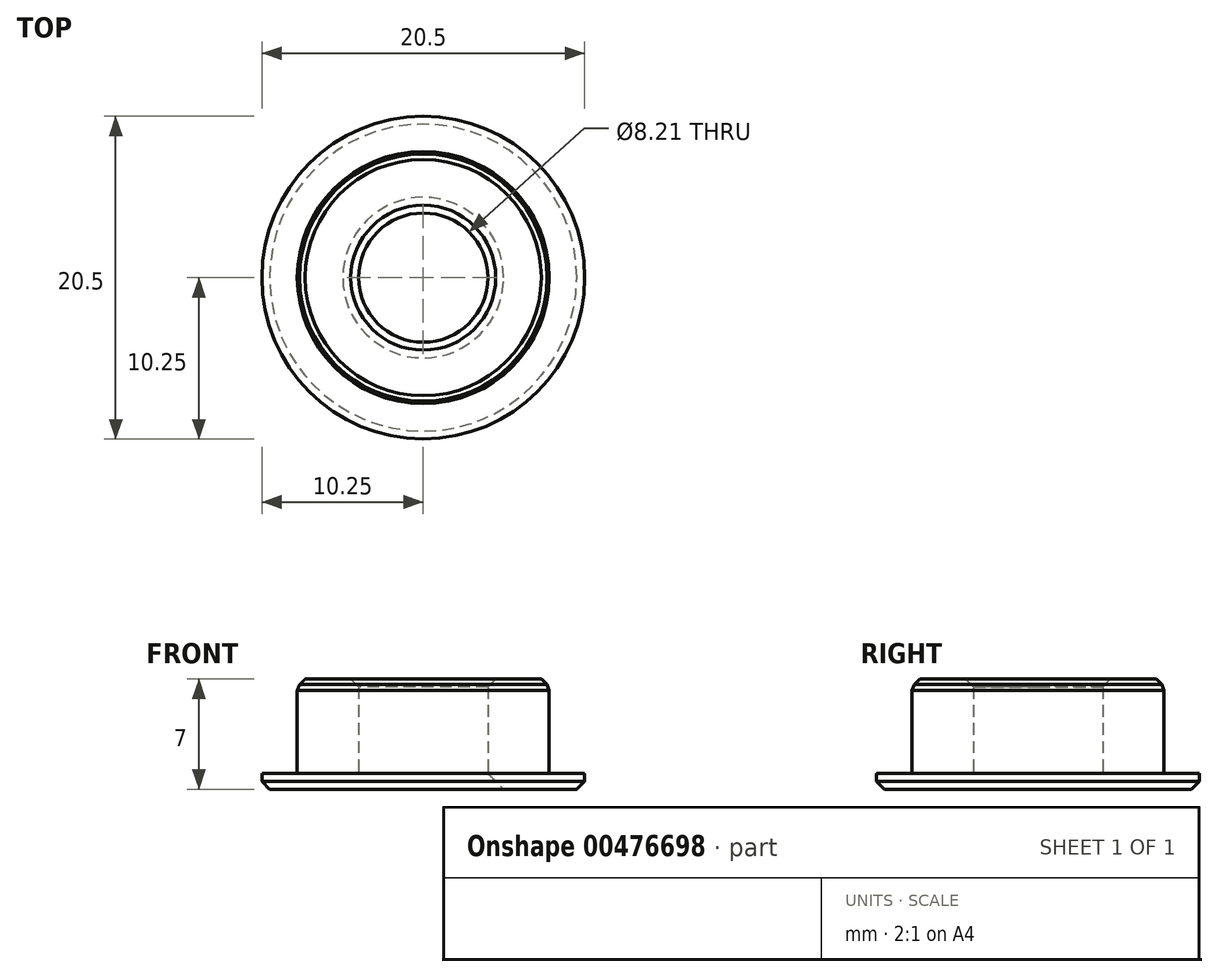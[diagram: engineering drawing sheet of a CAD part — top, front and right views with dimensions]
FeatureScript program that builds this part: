
annotation { "Feature Type Name" : "Feature", "Feature Type Description" : "" }
export const myFeature = defineFeature(function(context is Context, id is Id, definition is map)
    precondition{}
    {
        {
            var Q0;
            Q0=qCreatedBy(makeId("Top.planeOp"),FACE);
            var sketch = newSketch(context, id + "F0", { "sketchPlane" : qUnion([Q0])});
            skCircle(sketch, "E0", {"center": v(0, 0) * mm, "radius": 4.1 * mm});
            skCircle(sketch, "E1", {"center": v(0, 0) * mm, "radius": 8 * mm});
            skCircle(sketch, "E2", {"center": v(0, 0) * mm, "radius": 10.25 * mm});
            skSolve(sketch);
        }
        {
            var Q0;
            Q0=makeQuery(id+"F0.imprint","IMPRINT",FACE,{"disambiguationData":[TD([[makeQuery(id+"F0.imprint","IMPRINT",EDGE,{"derivedFrom":sQuery(id+"F0.wireOp",EDGE,"E1")}),-1.0]])]});
            extrude(context, id + "F1", {"entities" : qUnion([Q0]), "depth" : 1 * mm});
        }
        {
            var Q0;
            Q0=makeQuery(id+"F0.imprint","IMPRINT",FACE,{"disambiguationData":[TD([[makeQuery(id+"F0.imprint","IMPRINT",EDGE,{"derivedFrom":sQuery(id+"F0.wireOp",EDGE,"E0")}),-1.0]])]});
            extrude(context, id + "F2", {"entities" : qUnion([Q0]), "operationType" : NewBodyOperationType.ADD, "depth" : 7 * mm});
        }
        {
            var Q0;
            Q0=makeQuery(id+"F1.opExtrude","CAP_EDGE",EDGE,{"disambiguationData":[OSD([sQuery(id+"F0.wireOp",EDGE,"E2")])],"isStart":true});
            var Q1;
            Q1=makeQuery(id+"F2.opExtrude","CAP_EDGE",EDGE,{"disambiguationData":[OSD([sQuery(id+"F0.wireOp",EDGE,"E0")])],"isStart":false});
            chamfer(context, id + "F3", {"entities" : qUnion([Q0, Q1]), "width" : .5 * mm, "tangentPropagation" : true});
        }
        {
            var Q0;
            Q0=makeQuery(id+"F2.opExtrude","CAP_EDGE",EDGE,{"disambiguationData":[OSD([sQuery(id+"F0.wireOp",EDGE,"E1")])],"isStart":false});
            chamfer(context, id + "F4", {"entities" : qUnion([Q0]), "width" : .5 * mm, "tangentPropagation" : true});
        }
        {
            var Q0;
            {var subQ0=sQuery(id+"F0.wireOp",EDGE,"E1");Q0=makeQuery(id+"F4.opChamfer","BLEND_EDGE",EDGE,{"blendedFrom":[makeQuery(id+"F2.opExtrude","CAP_EDGE",EDGE,{"disambiguationData":[OSD([subQ0])],"isStart":false}),makeQuery(id+"F2.opExtrude","SWEPT_FACE",FACE,{"disambiguationData":[OSD([subQ0])]})],"blendedInto":[makeQuery(id+"F2.opExtrude","SWEPT_FACE",FACE,{"disambiguationData":[OSD([subQ0])]})]});}
            chamfer(context, id + "F5", {"entities" : qUnion([Q0]), "width" : .5 * mm, "tangentPropagation" : true});
        }
        {
            var Q0;
            Q0=makeQuery(id+"F2.opExtrude","CAP_EDGE",EDGE,{"disambiguationData":[OSD([sQuery(id+"F0.wireOp",EDGE,"E0")])],"isStart":true});
            chamfer(context, id + "F6", {"entities" : qUnion([Q0]), "width" : 1 * mm, "tangentPropagation" : true});
        }
    });
